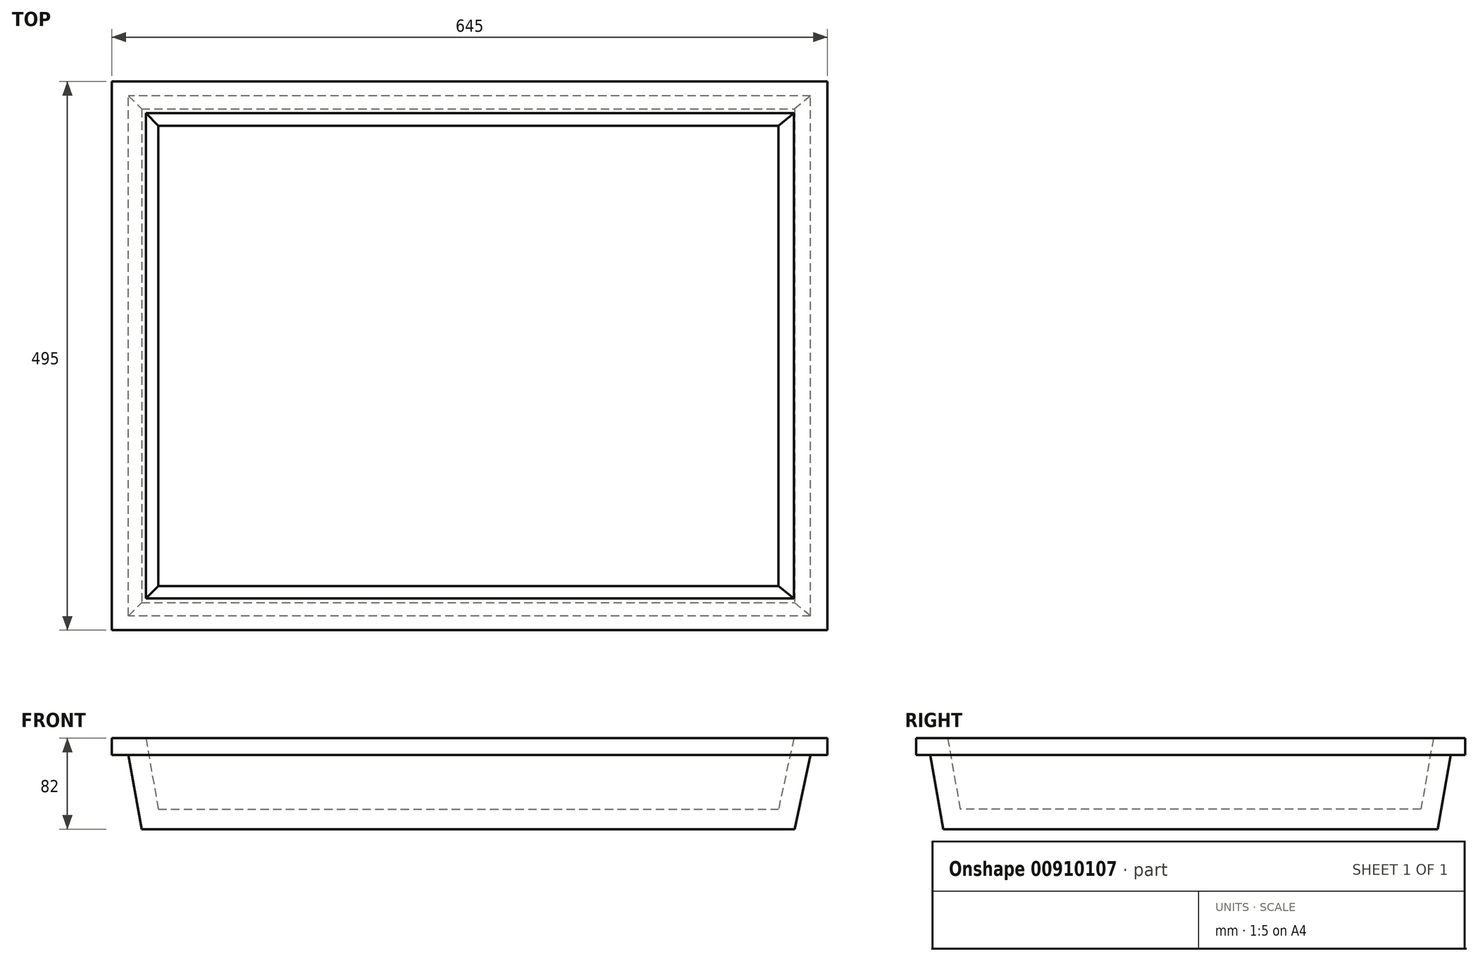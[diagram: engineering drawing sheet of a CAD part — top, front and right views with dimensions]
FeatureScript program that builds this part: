
annotation { "Feature Type Name" : "Feature", "Feature Type Description" : "" }
export const myFeature = defineFeature(function(context is Context, id is Id, definition is map)
    precondition{}
    {
        {
            var Q0;
            Q0=qCreatedBy(makeId("Top.planeOp"),FACE);
            var sketch = newSketch(context, id + "F0", { "sketchPlane" : qUnion([Q0])});
            skLineSegment(sketch, "E0.bottom", {"start": v(-322.5, -247.5) * mm, "end": v(322.5, -247.5) * mm});
            skLineSegment(sketch, "E0.top", {"start": v(-322.5, 247.5) * mm, "end": v(322.5, 247.5) * mm});
            skLineSegment(sketch, "E0.left", {"start": v(-322.5, -247.5) * mm, "end": v(-322.5, 247.5) * mm});
            skLineSegment(sketch, "E0.right", {"start": v(322.5, -247.5) * mm, "end": v(322.5, 247.5) * mm});
            skSolve(sketch);
        }
        {
            var Q0;
            Q0=qSketchRegion(id+"F0",true);
            extrude(context, id + "F1", {"entities" : qUnion([Q0]), "oppositeDirection" : true, "depth" : 82 * mm, "offsetDistance" : 25 * mm});
        }
        {
            var Q0;
            Q0=qCreatedBy(makeId("Right.planeOp"),FACE);
            var sketch = newSketch(context, id + "F2", { "sketchPlane" : qUnion([Q0])});
            skLineSegment(sketch, "E1", {"start": v(-277.5, -112) * mm, "end": v(-217.5, -112) * mm});
            skLineSegment(sketch, "E2", {"start": v(-217.5, -112) * mm, "end": v(-234.6, -15) * mm});
            skLineSegment(sketch, "E3", {"start": v(-234.6, -15) * mm, "end": v(-277.5, -15) * mm});
            skLineSegment(sketch, "E4", {"start": v(-277.5, -15) * mm, "end": v(-277.5, -112) * mm});
            skLineSegment(sketch, "E5.MirrorCS", {"start": v(234.6, -15) * mm, "end": v(277.5, -15) * mm});
            skLineSegment(sketch, "E6.MirrorCS", {"start": v(217.5, -112) * mm, "end": v(234.6, -15) * mm});
            skLineSegment(sketch, "E7.MirrorCS", {"start": v(277.5, -15) * mm, "end": v(277.5, -112) * mm});
            skLineSegment(sketch, "E8.MirrorCS", {"start": v(277.5, -112) * mm, "end": v(217.5, -112) * mm});
            skSolve(sketch);
        }
        {
            var Q0;
            Q0=makeQuery(id+"F2.imprint","IMPRINT",FACE,{"disambiguationData":[TD([[makeQuery(id+"F2.imprint","IMPRINT",EDGE,{"derivedFrom":sQuery(id+"F2.wireOp",EDGE,"E1")}),1.0]])]});
            var Q1;
            Q1=makeQuery(id+"F2.imprint","IMPRINT",FACE,{"disambiguationData":[TD([[makeQuery(id+"F2.imprint","IMPRINT",EDGE,{"derivedFrom":sQuery(id+"F2.wireOp",EDGE,"E5.MirrorCS")}),-1.0]])]});
            extrude(context, id + "F3", {"entities" : qUnion([Q0, Q1]), "operationType" : NewBodyOperationType.REMOVE, "endBound" : BoundingType.THROUGH_ALL, "depth" : 25 * mm, "offsetDistance" : 25 * mm, "hasSecondDirection" : true, "secondDirectionOppositeDirection" : true, "secondDirectionDepth" : 495 * mm});
        }
        {
            var Q0;
            Q0=qCreatedBy(makeId("Front.planeOp"),FACE);
            var sketch = newSketch(context, id + "F4", { "sketchPlane" : qUnion([Q0])});
            skLineSegment(sketch, "E9", {"start": v(-337.5, -185.14) * mm, "end": v(-277.5, -185.14) * mm});
            skLineSegment(sketch, "E10", {"start": v(-277.5, -185.14) * mm, "end": v(-307.5, -15) * mm});
            skLineSegment(sketch, "E11", {"start": v(-307.5, -15) * mm, "end": v(-337.5, -15) * mm});
            skLineSegment(sketch, "E12", {"start": v(-337.5, -15) * mm, "end": v(-337.5, -185.14) * mm});
            skLineSegment(sketch, "E13.MirrorCS", {"start": v(307.5, -15) * mm, "end": v(337.5, -15) * mm});
            skLineSegment(sketch, "E14.MirrorCS", {"start": v(277.54, -154.36) * mm, "end": v(307.5, -15) * mm});
            skLineSegment(sketch, "E15.MirrorCS", {"start": v(337.5, -15) * mm, "end": v(337.5, -156.6) * mm});
            skLineSegment(sketch, "E16.MirrorCS", {"start": v(337.5, -156.6) * mm, "end": v(277.54, -154.36) * mm});
            skSolve(sketch);
        }
        {
            var Q0;
            Q0=qSketchRegion(id+"F4",true);
            extrude(context, id + "F5", {"entities" : qUnion([Q0]), "operationType" : NewBodyOperationType.REMOVE, "depth" : 365 * mm, "offsetDistance" : 25 * mm, "hasSecondDirection" : true, "secondDirectionOppositeDirection" : true, "secondDirectionDepth" : 341 * mm});
        }
        {
            var Q0;
            Q0=makeQuery(id+"F1.opExtrude","CAP_FACE",FACE,{"disambiguationData":[OSD([sQuery(id+"F0.wireOp",EDGE,"E0.bottom"),sQuery(id+"F0.wireOp",EDGE,"E0.top"),sQuery(id+"F0.wireOp",EDGE,"E0.left"),sQuery(id+"F0.wireOp",EDGE,"E0.right")])],"isStart":true});
            shell(context, id + "F6", {"entities" : qUnion([Q0]), "thickness" : 18 * mm});
        }
    });
